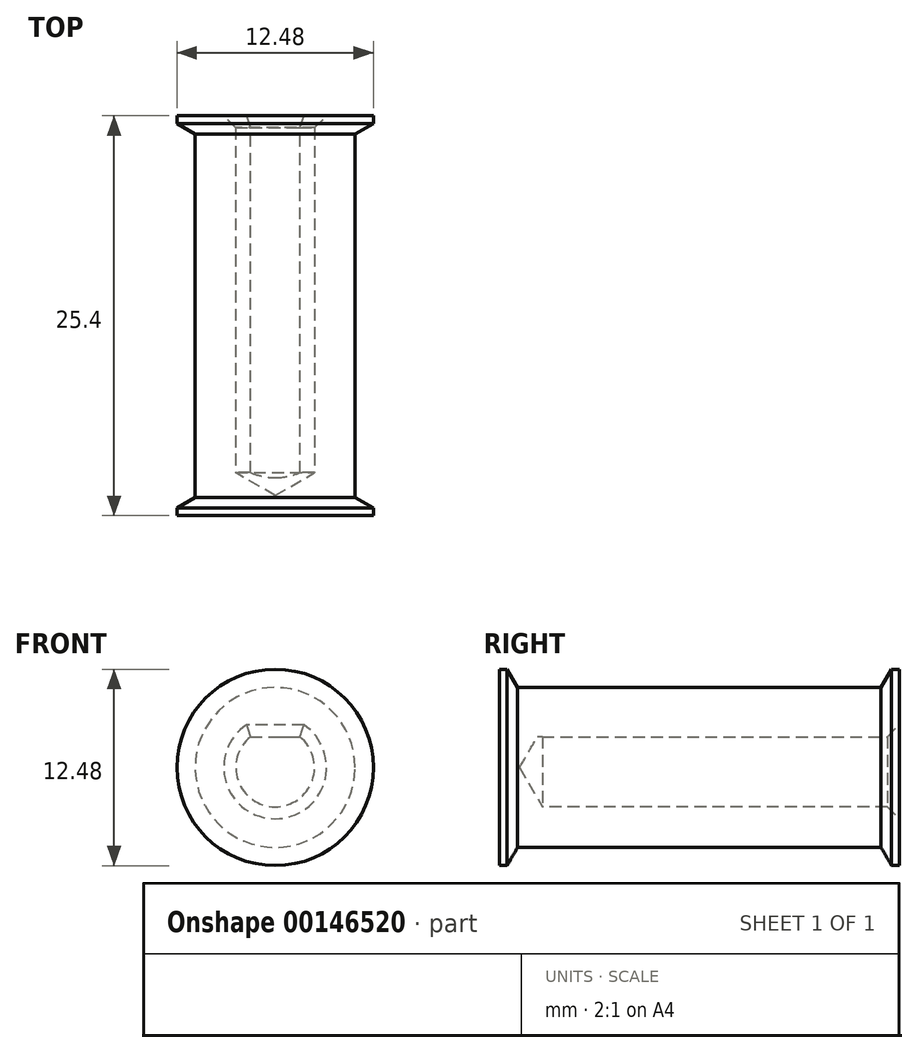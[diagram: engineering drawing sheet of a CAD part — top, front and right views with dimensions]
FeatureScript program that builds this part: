
annotation { "Feature Type Name" : "Feature", "Feature Type Description" : "" }
export const myFeature = defineFeature(function(context is Context, id is Id, definition is map)
    precondition{}
    {
        {
            var Q0;
            Q0=qCreatedBy(makeId("Top.planeOp"),FACE);
            var sketch = newSketch(context, id + "F0", { "sketchPlane" : qUnion([Q0])});
            skLineSegment(sketch, "E0", {"start": v(2.5, -25.4) * mm, "end": v(6.24, -25.4) * mm});
            skLineSegment(sketch, "E1", {"start": v(6.24, -25.4) * mm, "end": v(6.24, -24.91) * mm});
            skLineSegment(sketch, "E2", {"start": v(6.24, -24.91) * mm, "end": v(5.08, -24.24) * mm});
            skLineSegment(sketch, "E3", {"start": v(5.08, -24.24) * mm, "end": v(5.08, -1.16) * mm});
            skLineSegment(sketch, "E4", {"start": v(5.08, -1.16) * mm, "end": v(6.24, -0.49) * mm});
            skLineSegment(sketch, "E5", {"start": v(6.24, -0.49) * mm, "end": v(6.24, 0) * mm});
            skLineSegment(sketch, "E6", {"start": v(6.24, 0) * mm, "end": v(2.5, 0) * mm});
            skLineSegment(sketch, "E7", {"start": v(2.5, 0) * mm, "end": v(2.5, -25.4) * mm});
            skLineSegment(sketch, "E8", {"start": v(2.5, -22.67) * mm, "end": v(0, -24.11) * mm});
            skLineSegment(sketch, "E9", {"start": v(0, -24.11) * mm, "end": v(0, -25.4) * mm});
            skLineSegment(sketch, "E10", {"start": v(0, -25.4) * mm, "end": v(2.5, -25.4) * mm});
            skPoint(sketch, "E11", {"position": v(2.5, -12.7) * mm});
            skPoint(sketch, "E12", {"position": v(5.08, -12.7) * mm});
            skLineSegment(sketch, "E13", {"start": v(5.08, -25.4) * mm, "end": v(5.08, -24.24) * mm, "construction": true});
            skLineSegment(sketch, "E14", {"start": v(5.08, -24.24) * mm, "end": v(6.24, -24.24) * mm, "construction": true});
            skLineSegment(sketch, "E15", {"start": v(0, -24.11) * mm, "end": v(0, 0) * mm, "construction": true});
            skSolve(sketch);
        }
        {
            var Q0;
            {var subQ2=sQuery(id+"F0.wireOp",EDGE,"E8");Q0=makeQuery(id+"F0.imprint","IMPRINT",FACE,{"disambiguationData":[TD([[makeQuery(id+"F0.imprint","IMPRINT",EDGE,{"derivedFrom":subQ2}),1.0]])]});}
            var Q1;
            {var subQ1=sQuery(id+"F0.wireOp",EDGE,"E0");Q1=makeQuery(id+"F0.imprint","IMPRINT",FACE,{"disambiguationData":[TD([[makeQuery(id+"F0.imprint","IMPRINT",EDGE,{"derivedFrom":subQ1}),1.0]])]});}
            var Q2;
            Q2=sQuery(id+"F0.wireOp",EDGE,"E15");
            revolve(context, id + "F1", {"entities" : qUnion([Q0, Q1]), "axis" : qUnion([Q2]), "revolveType" : RevolveType.FULL});
        }
        {
            var Q0;
            Q0=makeQuery(id+"F1.opRevolve","SWEPT_FACE",FACE,{"disambiguationData":[OSD([sQuery(id+"F0.wireOp",EDGE,"E6")])]});
            var sketch = newSketch(context, id + "F2", { "sketchPlane" : qUnion([Q0])});
            skLineSegment(sketch, "E16", {"start": v(-1.57, 1.94) * mm, "end": v(1.57, 1.94) * mm});
            skArc(sketch, "E17", {"start": v(-1.57, 1.94) * mm, "mid": v(0, 2.5) * mm, "end": v(1.57, 1.94) * mm});
            skSolve(sketch);
        }
        {
            var Q0;
            Q0=makeQuery(id+"F2.imprint","IMPRINT",FACE,{"disambiguationData":[TD([[makeQuery(id+"F2.imprint","IMPRINT",EDGE,{"derivedFrom":sQuery(id+"F2.wireOp",EDGE,"E16")}),1.0]])]});
            extrude(context, id + "F3", {"entities" : qUnion([Q0]), "operationType" : NewBodyOperationType.ADD, "endBound" : BoundingType.UP_TO_NEXT, "oppositeDirection" : true, "depth" : 25.4 * mm});
        }
        {
            var Q0;
            Q0=makeQuery(id+"F1.opRevolve","SWEPT_EDGE",EDGE,{"disambiguationData":[OSD([sQuery(id+"F0.wireOp",EDGE,"E6"),sQuery(id+"F0.wireOp",EDGE,"E7")])]});
            var Q1;
            Q1=makeQuery(id+"F3.opExtrude","CAP_EDGE",EDGE,{"disambiguationData":[OSD([sQuery(id+"F2.wireOp",EDGE,"E16")])],"isStart":true});
            chamfer(context, id + "F4", {"entities" : qUnion([Q0, Q1]), "width" : 0.76 * mm, "tangentPropagation" : true});
        }
    });
